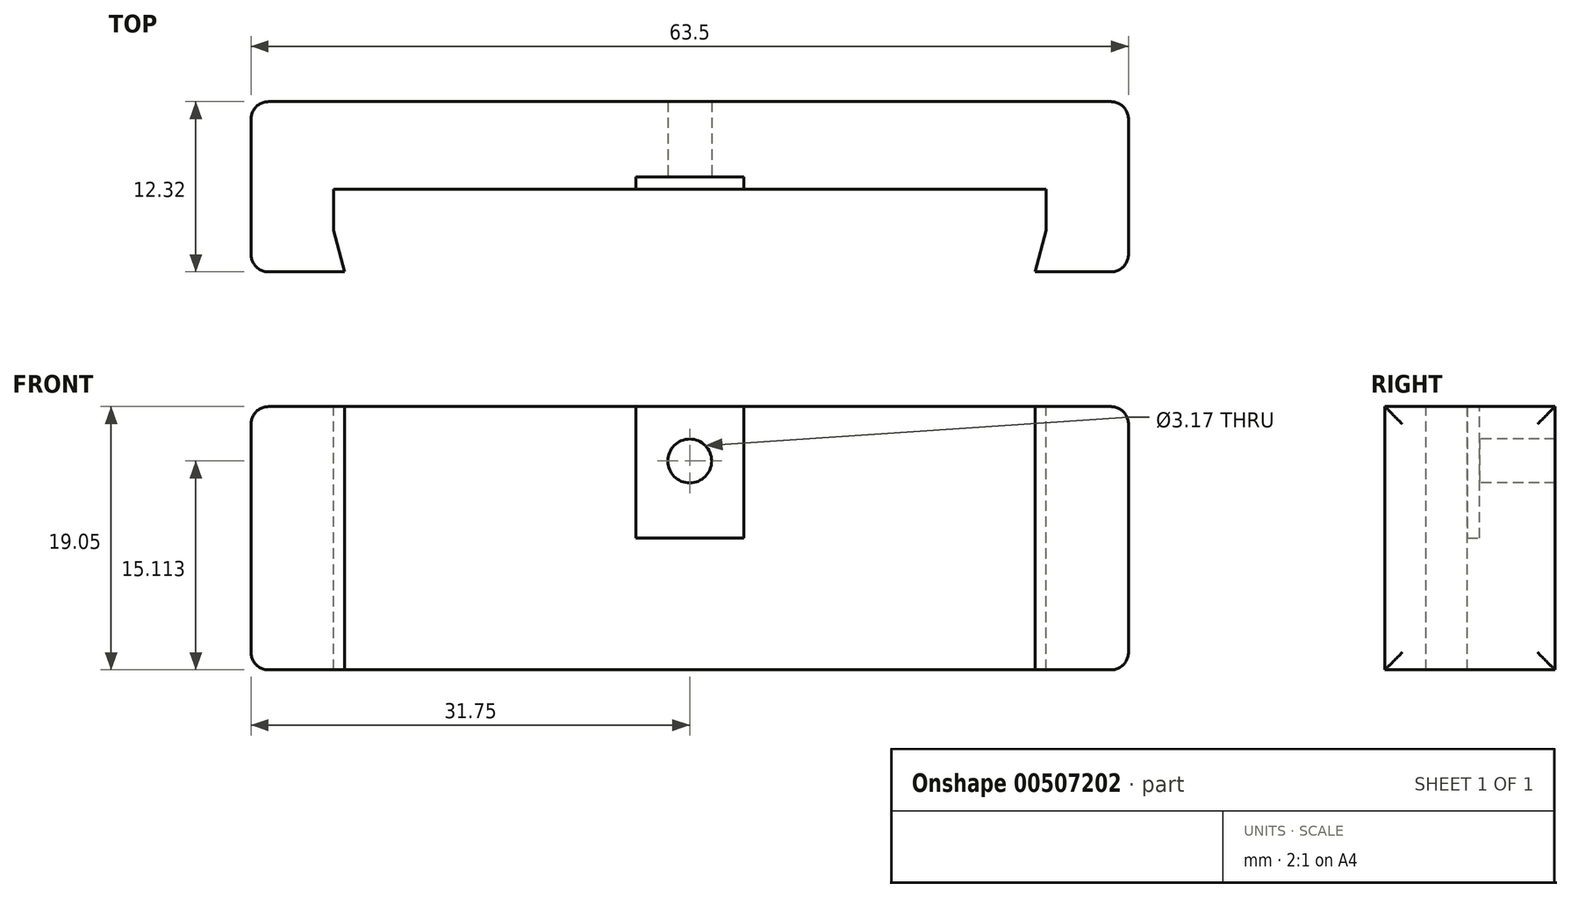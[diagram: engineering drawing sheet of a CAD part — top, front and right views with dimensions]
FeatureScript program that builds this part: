
annotation { "Feature Type Name" : "Feature", "Feature Type Description" : "" }
export const myFeature = defineFeature(function(context is Context, id is Id, definition is map)
    precondition{}
    {
        {
            var Q0;
            Q0=qCreatedBy(makeId("Top.planeOp"),FACE);
            var sketch = newSketch(context, id + "F0", { "sketchPlane" : qUnion([Q0])});
            skLineSegment(sketch, "E0.bottom", {"start": v(31.75, -6.16) * mm, "end": v(-31.75, -6.16) * mm});
            skLineSegment(sketch, "E0.top", {"start": v(31.75, 6.16) * mm, "end": v(-31.75, 6.16) * mm});
            skLineSegment(sketch, "E0.left", {"start": v(31.75, -6.16) * mm, "end": v(31.75, 6.16) * mm});
            skLineSegment(sketch, "E0.right", {"start": v(-31.75, -6.16) * mm, "end": v(-31.75, 6.16) * mm});
            skPoint(sketch, "E0.middle", {"position": v(0, 0) * mm});
            skSolve(sketch);
        }
        {
            var Q0;
            Q0=makeQuery(id+"F0.imprint","IMPRINT",FACE,{"disambiguationData":[TD([[makeQuery(id+"F0.imprint","IMPRINT",EDGE,{"derivedFrom":sQuery(id+"F0.wireOp",EDGE,"E0.bottom")}),-1.0]])]});
            extrude(context, id + "F1", {"entities" : qUnion([Q0]), "depth" : 19.05 * mm});
        }
        {
            var Q0;
            Q0=makeQuery(id+"F1.opExtrude","CAP_FACE",FACE,{"disambiguationData":[OSD([sQuery(id+"F0.wireOp",EDGE,"E0.bottom"),sQuery(id+"F0.wireOp",EDGE,"E0.top"),sQuery(id+"F0.wireOp",EDGE,"E0.left"),sQuery(id+"F0.wireOp",EDGE,"E0.right")])],"isStart":false});
            var sketch = newSketch(context, id + "F2", { "sketchPlane" : qUnion([Q0])});
            skLineSegment(sketch, "E1.bottom", {"start": v(25.78, -3.18) * mm, "end": v(-25.78, -3.18) * mm});
            skLineSegment(sketch, "E1.top", {"start": v(25.78, -0.2) * mm, "end": v(-25.78, -0.2) * mm});
            skLineSegment(sketch, "E1.left", {"start": v(25.78, -3.18) * mm, "end": v(25.78, -0.2) * mm});
            skLineSegment(sketch, "E1.right", {"start": v(-25.78, -3.18) * mm, "end": v(-25.78, -0.2) * mm});
            skPoint(sketch, "E1.middle", {"position": v(0, -1.68) * mm});
            skLineSegment(sketch, "E2", {"start": v(0, 6.16) * mm, "end": v(0, -6.16) * mm, "construction": true});
            skLineSegment(sketch, "E3", {"start": v(-25.78, -3.18) * mm, "end": v(-24.98, -6.16) * mm});
            skLineSegment(sketch, "E4", {"start": v(-24.98, -6.16) * mm, "end": v(0, -6.16) * mm});
            skLineSegment(sketch, "E5.MirrorCS", {"start": v(25.78, -3.18) * mm, "end": v(24.98, -6.16) * mm});
            skLineSegment(sketch, "E6.MirrorCS", {"start": v(24.98, -6.16) * mm, "end": v(0, -6.16) * mm});
            skSolve(sketch);
        }
        {
            var Q0;
            Q0 = qSketchRegion(id + "F2", true);
            extrude(context, id + "F3", {"entities" : qUnion([Q0]), "operationType" : NewBodyOperationType.REMOVE, "oppositeDirection" : true, "depth" : 25.4 * mm});
        }
        {
            var Q0;
            Q0=makeQuery(id+"F1.opExtrude","CAP_FACE",FACE,{"disambiguationData":[OSD([sQuery(id+"F0.wireOp",EDGE,"E0.bottom"),sQuery(id+"F0.wireOp",EDGE,"E0.top"),sQuery(id+"F0.wireOp",EDGE,"E0.left"),sQuery(id+"F0.wireOp",EDGE,"E0.right")])],"isStart":false});
            var sketch = newSketch(context, id + "F4", { "sketchPlane" : qUnion([Q0])});
            skLineSegment(sketch, "E7.bottom", {"start": v(3.9, -1.08) * mm, "end": v(-3.9, -1.08) * mm});
            skLineSegment(sketch, "E7.top", {"start": v(3.9, 0.7) * mm, "end": v(-3.9, 0.7) * mm});
            skLineSegment(sketch, "E7.left", {"start": v(3.9, -1.08) * mm, "end": v(3.9, 0.7) * mm});
            skLineSegment(sketch, "E7.right", {"start": v(-3.9, -1.08) * mm, "end": v(-3.9, 0.7) * mm});
            skPoint(sketch, "E7.middle", {"position": v(0, -0.2) * mm});
            skSolve(sketch);
        }
        {
            var Q0;
            Q0 = qSketchRegion(id + "F4", true);
            extrude(context, id + "F5", {"entities" : qUnion([Q0]), "operationType" : NewBodyOperationType.REMOVE, "oppositeDirection" : true, "depth" : 9.52 * mm});
        }
        {
            var Q0;
            Q0=makeQuery(id+"F3.boolean.opBoolean","COPY",FACE,{"derivedFrom":makeQuery(id+"F3.opExtrude","SWEPT_FACE",FACE,{"disambiguationData":[OSD([sQuery(id+"F2.wireOp",EDGE,"E1.top")])]})});
            var sketch = newSketch(context, id + "F6", { "sketchPlane" : qUnion([Q0])});
            skCircle(sketch, "E8", {"center": v(0, 15.11) * mm, "radius": 1.59 * mm});
            skSolve(sketch);
        }
        {
            var Q0;
            Q0 = qSketchRegion(id + "F6", true);
            extrude(context, id + "F7", {"entities" : qUnion([Q0]), "operationType" : NewBodyOperationType.REMOVE, "oppositeDirection" : true, "depth" : 25.4 * mm});
        }
        {
            var Q0;
            Q0=makeQuery(id+"F1.opExtrude","SWEPT_EDGE",EDGE,{"disambiguationData":[OSD([sQuery(id+"F0.wireOp",EDGE,"E0.top"),sQuery(id+"F0.wireOp",EDGE,"E0.left")])]});
            var Q1;
            Q1=makeQuery(id+"F1.opExtrude","CAP_EDGE",EDGE,{"disambiguationData":[OSD([sQuery(id+"F0.wireOp",EDGE,"E0.right")])],"isStart":true});
            var Q2;
            Q2=makeQuery(id+"F1.opExtrude","SWEPT_EDGE",EDGE,{"disambiguationData":[OSD([sQuery(id+"F0.wireOp",EDGE,"E0.bottom"),sQuery(id+"F0.wireOp",EDGE,"E0.right")])]});
            var Q3;
            Q3=makeQuery(id+"F1.opExtrude","SWEPT_EDGE",EDGE,{"disambiguationData":[OSD([sQuery(id+"F0.wireOp",EDGE,"E0.bottom"),sQuery(id+"F0.wireOp",EDGE,"E0.left")])]});
            var Q4;
            Q4=makeQuery(id+"F1.opExtrude","CAP_EDGE",EDGE,{"disambiguationData":[OSD([sQuery(id+"F0.wireOp",EDGE,"E0.left")])],"isStart":true});
            var Q5;
            Q5=makeQuery(id+"F1.opExtrude","CAP_EDGE",EDGE,{"disambiguationData":[OSD([sQuery(id+"F0.wireOp",EDGE,"E0.right")])],"isStart":false});
            var Q6;
            Q6=makeQuery(id+"F1.opExtrude","SWEPT_FACE",FACE,{"disambiguationData":[OSD([sQuery(id+"F0.wireOp",EDGE,"E0.left")])]});
            var Q7;
            Q7=makeQuery(id+"F1.opExtrude","SWEPT_EDGE",EDGE,{"disambiguationData":[OSD([sQuery(id+"F0.wireOp",EDGE,"E0.top"),sQuery(id+"F0.wireOp",EDGE,"E0.right")])]});
            fillet(context, id + "F8", {"entities" : qUnion([Q0, Q1, Q2, Q3, Q4, Q5, Q6, Q7]), "radius" : 1.27 * mm, "tangentPropagation" : true, "allowEdgeOverflow" : false});
        }
    });
